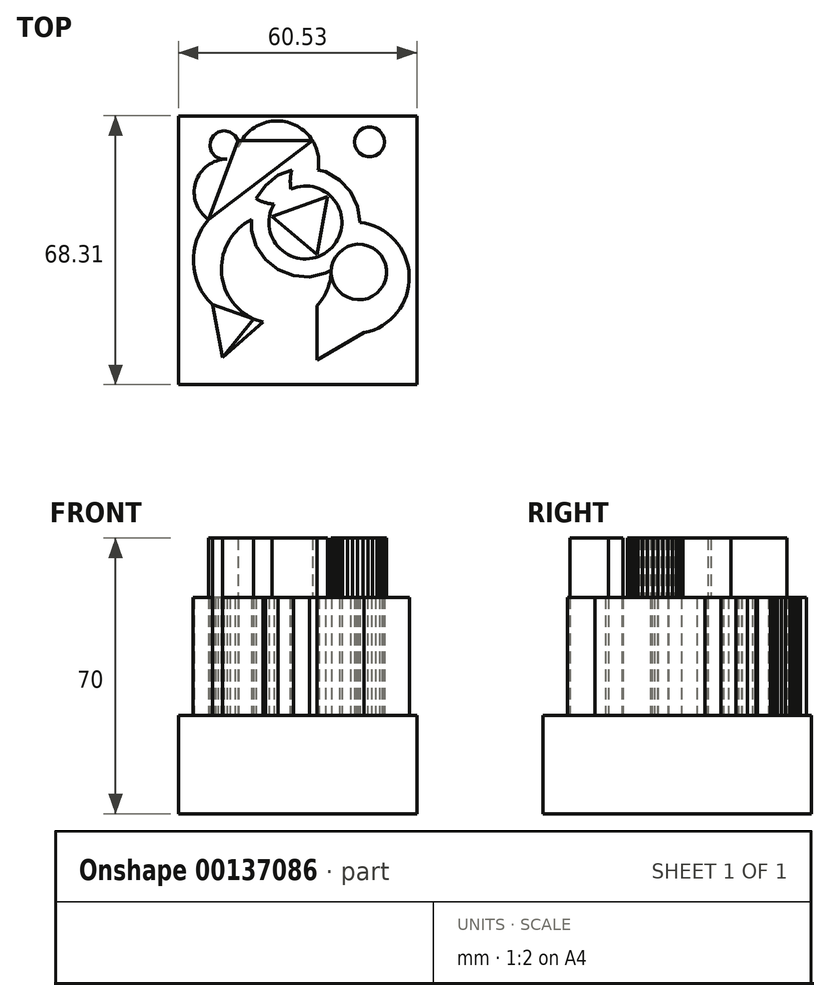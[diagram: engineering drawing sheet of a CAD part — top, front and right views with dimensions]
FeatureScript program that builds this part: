
annotation { "Feature Type Name" : "Feature", "Feature Type Description" : "" }
export const myFeature = defineFeature(function(context is Context, id is Id, definition is map)
    precondition{}
    {
        {
            var Q0;
            Q0=qCreatedBy(makeId("Top.planeOp"),FACE);
            var sketch = newSketch(context, id + "F0", { "sketchPlane" : qUnion([Q0])});
            skLineSegment(sketch, "E0.bottom", {"start": v(-67, 68.3) * mm, "end": v(-6.46, 68.3) * mm});
            skLineSegment(sketch, "E0.top", {"start": v(-67, 0) * mm, "end": v(-6.46, 0) * mm});
            skLineSegment(sketch, "E0.left", {"start": v(-67, 68.3) * mm, "end": v(-67, 0) * mm});
            skLineSegment(sketch, "E0.right", {"start": v(-6.46, 68.3) * mm, "end": v(-6.46, 0) * mm});
            skSolve(sketch);
        }
        {
            var Q0;
            Q0 = qSketchRegion(id + "F0", true);
            extrude(context, id + "F1", {"entities" : qUnion([Q0]), "depth" : 25 * mm});
        }
        {
            var Q0;
            Q0=makeQuery(id+"F1.opExtrude","CAP_FACE",FACE,{"disambiguationData":[OSD([sQuery(id+"F0.wireOp",EDGE,"E0.bottom"),sQuery(id+"F0.wireOp",EDGE,"E0.top"),sQuery(id+"F0.wireOp",EDGE,"E0.left"),sQuery(id+"F0.wireOp",EDGE,"E0.right")])],"isStart":false});
            var sketch = newSketch(context, id + "F2", { "sketchPlane" : qUnion([Q0])});
            skCircle(sketch, "E1.cCircle", {"center": v(-34.76, 41.21) * mm, "radius": 13.7 * mm, "construction": true});
            skLineSegment(sketch, "E1.0", {"start": v(-48.46, 39.15) * mm, "end": v(-48.46, 43.28) * mm});
            skLineSegment(sketch, "E1.1", {"start": v(-48.46, 43.28) * mm, "end": v(-47.24, 47.23) * mm});
            skLineSegment(sketch, "E1.2", {"start": v(-47.24, 47.23) * mm, "end": v(-44.92, 50.64) * mm});
            skLineSegment(sketch, "E1.3", {"start": v(-44.92, 50.64) * mm, "end": v(-41.69, 53.21) * mm});
            skLineSegment(sketch, "E1.4", {"start": v(-41.69, 53.21) * mm, "end": v(-37.84, 54.72) * mm});
            skLineSegment(sketch, "E1.5", {"start": v(-37.84, 54.72) * mm, "end": v(-33.72, 55.03) * mm});
            skLineSegment(sketch, "E1.6", {"start": v(-33.72, 55.03) * mm, "end": v(-29.7, 54.11) * mm});
            skLineSegment(sketch, "E1.7", {"start": v(-29.7, 54.11) * mm, "end": v(-26.12, 52.05) * mm});
            skLineSegment(sketch, "E1.8", {"start": v(-26.12, 52.05) * mm, "end": v(-23.3, 49.02) * mm});
            skLineSegment(sketch, "E1.9", {"start": v(-23.3, 49.02) * mm, "end": v(-21.51, 45.3) * mm});
            skLineSegment(sketch, "E1.10", {"start": v(-21.51, 45.3) * mm, "end": v(-20.9, 41.21) * mm});
            skLineSegment(sketch, "E1.11", {"start": v(-20.9, 41.21) * mm, "end": v(-21.51, 37.13) * mm});
            skLineSegment(sketch, "E1.12", {"start": v(-21.51, 37.13) * mm, "end": v(-23.3, 33.4) * mm});
            skLineSegment(sketch, "E1.13", {"start": v(-23.3, 33.4) * mm, "end": v(-26.12, 30.38) * mm});
            skLineSegment(sketch, "E1.14", {"start": v(-26.12, 30.38) * mm, "end": v(-29.7, 28.31) * mm});
            skLineSegment(sketch, "E1.15", {"start": v(-29.7, 28.31) * mm, "end": v(-33.72, 27.4) * mm});
            skLineSegment(sketch, "E1.16", {"start": v(-33.72, 27.4) * mm, "end": v(-37.84, 27.7) * mm});
            skLineSegment(sketch, "E1.17", {"start": v(-37.84, 27.7) * mm, "end": v(-41.69, 29.2) * mm});
            skLineSegment(sketch, "E1.18", {"start": v(-41.69, 29.2) * mm, "end": v(-44.92, 31.79) * mm});
            skLineSegment(sketch, "E1.19", {"start": v(-44.92, 31.79) * mm, "end": v(-47.24, 35.2) * mm});
            skLineSegment(sketch, "E1.20", {"start": v(-47.24, 35.2) * mm, "end": v(-48.46, 39.15) * mm});
            skPoint(sketch, "E1.0.midPoint", {"position": v(-48.46, 41.21) * mm});
            skCircle(sketch, "E2.cCircle", {"center": v(-53.23, 14.4) * mm, "radius": 3.94 * mm, "construction": true});
            skLineSegment(sketch, "E2.0", {"start": v(-45.49, 15.9) * mm, "end": v(-55.8, 6.95) * mm});
            skLineSegment(sketch, "E2.1", {"start": v(-55.8, 6.95) * mm, "end": v(-58.4, 20.36) * mm});
            skLineSegment(sketch, "E2.2", {"start": v(-58.4, 20.36) * mm, "end": v(-45.49, 15.9) * mm});
            skPoint(sketch, "E2.0.midPoint", {"position": v(-50.65, 11.42) * mm});
            skCircle(sketch, "E3.cCircle", {"center": v(-27.8, 13.2) * mm, "radius": 3.97 * mm, "construction": true});
            skLineSegment(sketch, "E3.0", {"start": v(-31.78, 6.33) * mm, "end": v(-31.78, 20.09) * mm});
            skLineSegment(sketch, "E3.1", {"start": v(-31.78, 20.09) * mm, "end": v(-19.86, 13.2) * mm});
            skLineSegment(sketch, "E3.2", {"start": v(-19.86, 13.2) * mm, "end": v(-31.78, 6.33) * mm});
            skPoint(sketch, "E3.0.midPoint", {"position": v(-31.78, 13.2) * mm});
            skCircle(sketch, "E4.cCircle", {"center": v(-55.41, 60.87) * mm, "radius": 3.58 * mm, "construction": true});
            skLineSegment(sketch, "E4.0", {"start": v(-54.65, 57.3) * mm, "end": v(-56.17, 57.3) * mm});
            skLineSegment(sketch, "E4.1", {"start": v(-56.17, 57.3) * mm, "end": v(-57.56, 57.92) * mm});
            skLineSegment(sketch, "E4.2", {"start": v(-57.56, 57.92) * mm, "end": v(-58.58, 59.05) * mm});
            skLineSegment(sketch, "E4.3", {"start": v(-58.58, 59.05) * mm, "end": v(-59.05, 60.5) * mm});
            skLineSegment(sketch, "E4.4", {"start": v(-59.05, 60.5) * mm, "end": v(-58.89, 62) * mm});
            skLineSegment(sketch, "E4.5", {"start": v(-58.89, 62) * mm, "end": v(-58.13, 63.32) * mm});
            skLineSegment(sketch, "E4.6", {"start": v(-58.13, 63.32) * mm, "end": v(-56.9, 64.21) * mm});
            skLineSegment(sketch, "E4.7", {"start": v(-56.9, 64.21) * mm, "end": v(-55.41, 64.53) * mm});
            skLineSegment(sketch, "E4.8", {"start": v(-55.41, 64.53) * mm, "end": v(-53.93, 64.21) * mm});
            skLineSegment(sketch, "E4.9", {"start": v(-53.93, 64.21) * mm, "end": v(-52.7, 63.32) * mm});
            skLineSegment(sketch, "E4.10", {"start": v(-52.7, 63.32) * mm, "end": v(-51.94, 62) * mm});
            skLineSegment(sketch, "E4.11", {"start": v(-51.94, 62) * mm, "end": v(-51.78, 60.5) * mm});
            skLineSegment(sketch, "E4.12", {"start": v(-51.78, 60.5) * mm, "end": v(-52.25, 59.05) * mm});
            skLineSegment(sketch, "E4.13", {"start": v(-52.25, 59.05) * mm, "end": v(-53.26, 57.92) * mm});
            skLineSegment(sketch, "E4.14", {"start": v(-53.26, 57.92) * mm, "end": v(-54.65, 57.3) * mm});
            skPoint(sketch, "E4.0.midPoint", {"position": v(-55.41, 57.3) * mm});
            skCircle(sketch, "E5.cCircle", {"center": v(-18.47, 61.67) * mm, "radius": 3.77 * mm, "construction": true});
            skLineSegment(sketch, "E5.0", {"start": v(-17.93, 57.9) * mm, "end": v(-19.01, 57.9) * mm});
            skLineSegment(sketch, "E5.1", {"start": v(-19.01, 57.9) * mm, "end": v(-20.05, 58.2) * mm});
            skLineSegment(sketch, "E5.2", {"start": v(-20.05, 58.2) * mm, "end": v(-20.97, 58.79) * mm});
            skLineSegment(sketch, "E5.3", {"start": v(-20.97, 58.79) * mm, "end": v(-21.68, 59.6) * mm});
            skLineSegment(sketch, "E5.4", {"start": v(-21.68, 59.6) * mm, "end": v(-22.13, 60.6) * mm});
            skLineSegment(sketch, "E5.5", {"start": v(-22.13, 60.6) * mm, "end": v(-22.28, 61.67) * mm});
            skLineSegment(sketch, "E5.6", {"start": v(-22.28, 61.67) * mm, "end": v(-22.13, 62.74) * mm});
            skLineSegment(sketch, "E5.7", {"start": v(-22.13, 62.74) * mm, "end": v(-21.68, 63.73) * mm});
            skLineSegment(sketch, "E5.8", {"start": v(-21.68, 63.73) * mm, "end": v(-20.97, 64.55) * mm});
            skLineSegment(sketch, "E5.9", {"start": v(-20.97, 64.55) * mm, "end": v(-20.05, 65.14) * mm});
            skLineSegment(sketch, "E5.10", {"start": v(-20.05, 65.14) * mm, "end": v(-19.01, 65.44) * mm});
            skLineSegment(sketch, "E5.11", {"start": v(-19.01, 65.44) * mm, "end": v(-17.93, 65.44) * mm});
            skLineSegment(sketch, "E5.12", {"start": v(-17.93, 65.44) * mm, "end": v(-16.89, 65.14) * mm});
            skLineSegment(sketch, "E5.13", {"start": v(-16.89, 65.14) * mm, "end": v(-15.97, 64.55) * mm});
            skLineSegment(sketch, "E5.14", {"start": v(-15.97, 64.55) * mm, "end": v(-15.26, 63.73) * mm});
            skLineSegment(sketch, "E5.15", {"start": v(-15.26, 63.73) * mm, "end": v(-14.81, 62.74) * mm});
            skLineSegment(sketch, "E5.16", {"start": v(-14.81, 62.74) * mm, "end": v(-14.66, 61.67) * mm});
            skLineSegment(sketch, "E5.17", {"start": v(-14.66, 61.67) * mm, "end": v(-14.81, 60.6) * mm});
            skLineSegment(sketch, "E5.18", {"start": v(-14.81, 60.6) * mm, "end": v(-15.26, 59.6) * mm});
            skLineSegment(sketch, "E5.19", {"start": v(-15.26, 59.6) * mm, "end": v(-15.97, 58.79) * mm});
            skLineSegment(sketch, "E5.20", {"start": v(-15.97, 58.79) * mm, "end": v(-16.89, 58.2) * mm});
            skLineSegment(sketch, "E5.21", {"start": v(-16.89, 58.2) * mm, "end": v(-17.93, 57.9) * mm});
            skPoint(sketch, "E5.0.midPoint", {"position": v(-18.47, 57.9) * mm});
            skCircle(sketch, "E6", {"center": v(-34.76, 41.21) * mm, "radius": 9.26 * mm});
            skArc(sketch, "E7", {"start": v(-47.24, 47.23) * mm, "mid": v(-62.07, 37.63) * mm, "end": v(-58.4, 20.36) * mm});
            skArc(sketch, "E8", {"start": v(-31.78, 20.09) * mm, "mid": v(-46.23, 42.8) * mm, "end": v(-45.49, 15.9) * mm});
            skArc(sketch, "E9", {"start": v(-19.86, 13.2) * mm, "mid": v(-8.38, 27.65) * mm, "end": v(-20.9, 41.21) * mm});
            skArc(sketch, "E10", {"start": v(-16.89, 58.2) * mm, "mid": v(-38.3, 54.29) * mm, "end": v(-20.9, 41.21) * mm});
            skArc(sketch, "E11", {"start": v(-47.24, 47.23) * mm, "mid": v(-32.2, 60.56) * mm, "end": v(-52.25, 59.05) * mm});
            skArc(sketch, "E12", {"start": v(-54.65, 57.3) * mm, "mid": v(-62.32, 45.54) * mm, "end": v(-48.46, 43.28) * mm});
            skArc(sketch, "E13", {"start": v(-55.8, 6.95) * mm, "mid": v(-43.92, 4.46) * mm, "end": v(-31.78, 4.87) * mm});
            skSolve(sketch);
        }
        {
            var Q0;
            Q0 = qSketchRegion(id + "F2", true);
            extrude(context, id + "F3", {"entities" : qUnion([Q0]), "operationType" : NewBodyOperationType.ADD, "depth" : 30 * mm});
        }
        {
            var Q0;
            Q0=makeQuery(id+"F3.opExtrude","CAP_FACE",FACE,{"disambiguationData":[OSD([sQuery(id+"F2.wireOp",EDGE,"E1.0"),sQuery(id+"F2.wireOp",EDGE,"E1.2"),sQuery(id+"F2.wireOp",EDGE,"E1.3"),sQuery(id+"F2.wireOp",EDGE,"E1.4"),sQuery(id+"F2.wireOp",EDGE,"E1.6"),sQuery(id+"F2.wireOp",EDGE,"E1.7"),sQuery(id+"F2.wireOp",EDGE,"E1.8"),sQuery(id+"F2.wireOp",EDGE,"E1.9"),sQuery(id+"F2.wireOp",EDGE,"E1.10"),sQuery(id+"F2.wireOp",EDGE,"E1.14"),sQuery(id+"F2.wireOp",EDGE,"E1.15"),sQuery(id+"F2.wireOp",EDGE,"E1.16"),sQuery(id+"F2.wireOp",EDGE,"E1.17"),sQuery(id+"F2.wireOp",EDGE,"E1.18"),sQuery(id+"F2.wireOp",EDGE,"E1.19"),sQuery(id+"F2.wireOp",EDGE,"E1.20"),sQuery(id+"F2.wireOp",EDGE,"E2.0"),sQuery(id+"F2.wireOp",EDGE,"E2.1"),sQuery(id+"F2.wireOp",EDGE,"E2.2"),sQuery(id+"F2.wireOp",EDGE,"E3.0"),sQuery(id+"F2.wireOp",EDGE,"E3.2"),sQuery(id+"F2.wireOp",EDGE,"E4.0"),sQuery(id+"F2.wireOp",EDGE,"E4.1"),sQuery(id+"F2.wireOp",EDGE,"E4.2"),sQuery(id+"F2.wireOp",EDGE,"E4.3"),sQuery(id+"F2.wireOp",EDGE,"E4.4"),sQuery(id+"F2.wireOp",EDGE,"E4.5"),sQuery(id+"F2.wireOp",EDGE,"E4.6"),sQuery(id+"F2.wireOp",EDGE,"E4.7"),sQuery(id+"F2.wireOp",EDGE,"E4.8"),sQuery(id+"F2.wireOp",EDGE,"E4.9"),sQuery(id+"F2.wireOp",EDGE,"E4.10"),sQuery(id+"F2.wireOp",EDGE,"E4.11"),sQuery(id+"F2.wireOp",EDGE,"E4.12"),sQuery(id+"F2.wireOp",EDGE,"E6"),sQuery(id+"F2.wireOp",EDGE,"E7"),sQuery(id+"F2.wireOp",EDGE,"E8"),sQuery(id+"F2.wireOp",EDGE,"E9"),sQuery(id+"F2.wireOp",EDGE,"E10"),sQuery(id+"F2.wireOp",EDGE,"E11"),sQuery(id+"F2.wireOp",EDGE,"E12")])],"isStart":false});
            var sketch = newSketch(context, id + "F4", { "sketchPlane" : qUnion([Q0])});
            skCircle(sketch, "E14.cCircle", {"center": v(-21.17, 28.62) * mm, "radius": 7.02 * mm, "construction": true});
            skLineSegment(sketch, "E14.0", {"start": v(-27.1, 32.45) * mm, "end": v(-26.26, 33.5) * mm});
            skLineSegment(sketch, "E14.1", {"start": v(-26.26, 33.5) * mm, "end": v(-25.25, 34.38) * mm});
            skLineSegment(sketch, "E14.2", {"start": v(-25.25, 34.38) * mm, "end": v(-24.08, 35.05) * mm});
            skLineSegment(sketch, "E14.3", {"start": v(-24.08, 35.05) * mm, "end": v(-22.81, 35.48) * mm});
            skLineSegment(sketch, "E14.4", {"start": v(-22.81, 35.48) * mm, "end": v(-21.49, 35.67) * mm});
            skLineSegment(sketch, "E14.5", {"start": v(-21.49, 35.67) * mm, "end": v(-20.15, 35.6) * mm});
            skLineSegment(sketch, "E14.6", {"start": v(-20.15, 35.6) * mm, "end": v(-18.84, 35.28) * mm});
            skLineSegment(sketch, "E14.7", {"start": v(-18.84, 35.28) * mm, "end": v(-17.62, 34.72) * mm});
            skLineSegment(sketch, "E14.8", {"start": v(-17.62, 34.72) * mm, "end": v(-16.53, 33.94) * mm});
            skLineSegment(sketch, "E14.9", {"start": v(-16.53, 33.94) * mm, "end": v(-15.61, 32.97) * mm});
            skLineSegment(sketch, "E14.10", {"start": v(-15.61, 32.97) * mm, "end": v(-14.89, 31.84) * mm});
            skLineSegment(sketch, "E14.11", {"start": v(-14.89, 31.84) * mm, "end": v(-14.4, 30.6) * mm});
            skLineSegment(sketch, "E14.12", {"start": v(-14.4, 30.6) * mm, "end": v(-14.14, 29.27) * mm});
            skLineSegment(sketch, "E14.13", {"start": v(-14.14, 29.27) * mm, "end": v(-14.15, 27.93) * mm});
            skLineSegment(sketch, "E14.14", {"start": v(-14.15, 27.93) * mm, "end": v(-14.4, 26.62) * mm});
            skLineSegment(sketch, "E14.15", {"start": v(-14.4, 26.62) * mm, "end": v(-14.9, 25.37) * mm});
            skLineSegment(sketch, "E14.16", {"start": v(-14.9, 25.37) * mm, "end": v(-15.63, 24.25) * mm});
            skLineSegment(sketch, "E14.17", {"start": v(-15.63, 24.25) * mm, "end": v(-16.56, 23.28) * mm});
            skLineSegment(sketch, "E14.18", {"start": v(-16.56, 23.28) * mm, "end": v(-17.66, 22.5) * mm});
            skLineSegment(sketch, "E14.19", {"start": v(-17.66, 22.5) * mm, "end": v(-18.88, 21.95) * mm});
            skLineSegment(sketch, "E14.20", {"start": v(-18.88, 21.95) * mm, "end": v(-20.18, 21.63) * mm});
            skLineSegment(sketch, "E14.21", {"start": v(-20.18, 21.63) * mm, "end": v(-21.52, 21.57) * mm});
            skLineSegment(sketch, "E14.22", {"start": v(-21.52, 21.57) * mm, "end": v(-22.85, 21.77) * mm});
            skLineSegment(sketch, "E14.23", {"start": v(-22.85, 21.77) * mm, "end": v(-24.12, 22.21) * mm});
            skLineSegment(sketch, "E14.24", {"start": v(-24.12, 22.21) * mm, "end": v(-25.28, 22.88) * mm});
            skLineSegment(sketch, "E14.25", {"start": v(-25.28, 22.88) * mm, "end": v(-26.29, 23.77) * mm});
            skLineSegment(sketch, "E14.26", {"start": v(-26.29, 23.77) * mm, "end": v(-27.11, 24.82) * mm});
            skLineSegment(sketch, "E14.27", {"start": v(-27.11, 24.82) * mm, "end": v(-27.73, 26.02) * mm});
            skLineSegment(sketch, "E14.28", {"start": v(-27.73, 26.02) * mm, "end": v(-28.1, 27.3) * mm});
            skLineSegment(sketch, "E14.29", {"start": v(-28.1, 27.3) * mm, "end": v(-28.22, 28.64) * mm});
            skLineSegment(sketch, "E14.30", {"start": v(-28.22, 28.64) * mm, "end": v(-28.1, 29.98) * mm});
            skLineSegment(sketch, "E14.31", {"start": v(-28.1, 29.98) * mm, "end": v(-27.71, 31.26) * mm});
            skLineSegment(sketch, "E14.32", {"start": v(-27.71, 31.26) * mm, "end": v(-27.1, 32.45) * mm});
            skPoint(sketch, "E14.0.midPoint", {"position": v(-26.68, 32.98) * mm});
            skCircle(sketch, "E15.cCircle", {"center": v(-34.76, 41.21) * mm, "radius": 4.3 * mm, "construction": true});
            skLineSegment(sketch, "E15.0", {"start": v(-31.85, 33.1) * mm, "end": v(-43.23, 42.75) * mm});
            skLineSegment(sketch, "E15.1", {"start": v(-43.23, 42.75) * mm, "end": v(-29.19, 47.78) * mm});
            skLineSegment(sketch, "E15.2", {"start": v(-29.19, 47.78) * mm, "end": v(-31.85, 33.1) * mm});
            skPoint(sketch, "E15.0.midPoint", {"position": v(-37.54, 37.93) * mm});
            skLineSegment(sketch, "E16", {"start": v(-32.95, 62) * mm, "end": v(-59.34, 41.98) * mm});
            skLineSegment(sketch, "E17", {"start": v(-59.34, 41.98) * mm, "end": v(-51.94, 62) * mm});
            skLineSegment(sketch, "E18", {"start": v(-51.94, 62) * mm, "end": v(-32.95, 62) * mm});
            skLineSegment(sketch, "E19", {"start": v(-55.35, 24.92) * mm, "end": v(-59.34, 41.98) * mm});
            skLineSegment(sketch, "E20", {"start": v(-58.4, 20.36) * mm, "end": v(-47.89, 16.72) * mm});
            skLineSegment(sketch, "E21", {"start": v(-47.89, 16.72) * mm, "end": v(-55.8, 6.95) * mm});
            skLineSegment(sketch, "E22", {"start": v(-55.8, 6.95) * mm, "end": v(-58.4, 20.36) * mm});
            skSolve(sketch);
        }
        {
            var Q0;
            Q0 = qSketchRegion(id + "F4", true);
            extrude(context, id + "F5", {"entities" : qUnion([Q0]), "operationType" : NewBodyOperationType.ADD, "depth" : 15 * mm});
        }
    });
